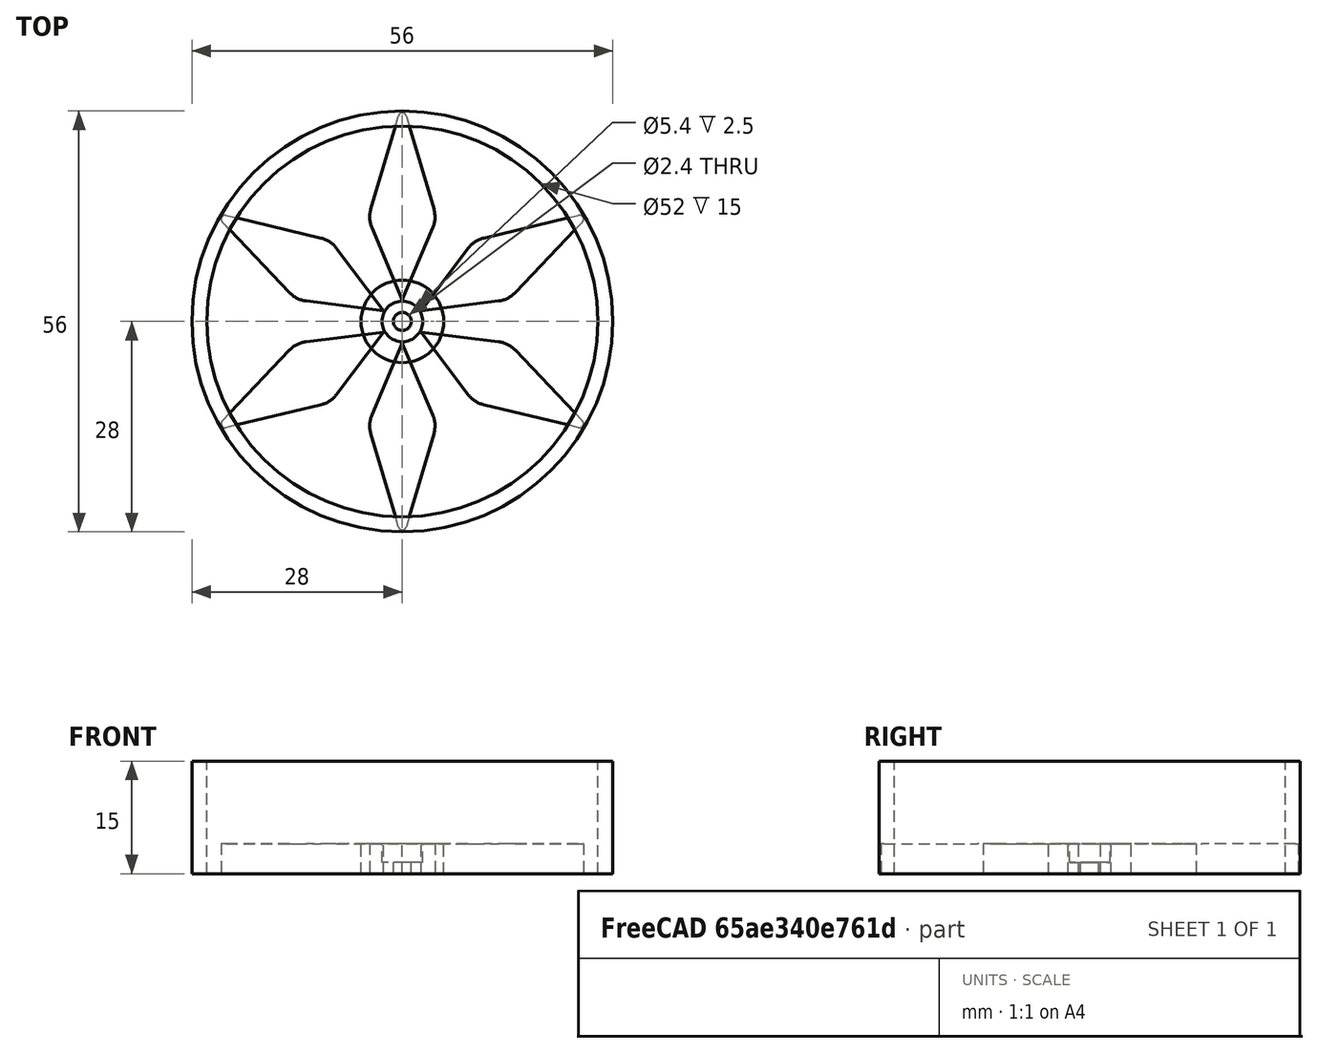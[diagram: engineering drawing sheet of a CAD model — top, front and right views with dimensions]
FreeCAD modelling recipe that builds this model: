
FCSTD DOCUMENT  (FreeCAD 0.16R6712 (Git))
Label: roda_romb
License: All rights reserved
LicenseURL: http://en.wikipedia.org/wiki/All_rights_reserved
objects: Part::Cylinder×5, Part::Cut×3, Sketcher::SketchObject×1, PartDesign::Pad×1, Part::FeaturePython×1
note: 12 computed .brp shape members not serialized (recipe doc carries the construction recipe); baked Part::Feature solids carry a one-line shape summary decoded from their .brp

FEATURE [Part::Cylinder] Cylinder  label="gross"
  Angle = 360
  Height = 4
  Placement = pos=(0,0,-1) rot=(0,0,1;0rad)
  Radius = 5.5
FEATURE [Part::Cylinder] Cylinder001  label="interior"
  Angle = 360
  Height = 6
  Placement = pos=(0,0,0.5) rot=(0,0,1;0rad)
  Radius = 2.7
FEATURE [Part::Cylinder] Cylinder002  label="Cylinder"
  Angle = 360
  Height = 7
  Placement = pos=(0,0,-1) rot=(0,0,1;0rad)
  Radius = 1.2
FEATURE [Part::Cut] Cut
  Base = -> Cylinder
  Tool = -> Cylinder002
FEATURE [Part::Cut] Cut001
  Base = -> Cut
  Placement = pos=(0,0,1) rot=(0,0,1;0rad)
  Tool = -> Cylinder001
FEATURE [Part::Cylinder] Cylinder004  label="fora_gran"
  Angle = 360
  Height = 15
  Placement = pos=(0,0,1) rot=(0,0,1;0rad)
  Radius = 28
FEATURE [Part::Cylinder] Cylinder005  label="forat_gran"
  Angle = 360
  Height = 15
  Placement = pos=(0,0,1) rot=(0,0,1;0rad)
  Radius = 26
FEATURE [Part::Cut] Cut002
  Base = -> Cylinder004
  Placement = pos=(0,0,-1) rot=(0,0,1;0rad)
  Tool = -> Cylinder005
FEATURE [Sketcher::SketchObject] Sketch
  sketch-geometry (7):
    g0: LineSegment StartX=0.518756 StartY=27.3536 StartZ=0 EndX=4.19558 EndY=14.9094 EndZ=0
    g1: LineSegment StartX=4.05671 StartY=12.4595 StartZ=0 EndX=0 EndY=2.87873 EndZ=0
    g2: LineSegment StartX=0 StartY=2.87873 StartZ=0 EndX=-4.05671 EndY=12.4595 EndZ=0
    g3: LineSegment StartX=-4.19558 StartY=14.9094 StartZ=0 EndX=-0.518756 EndY=27.3536 EndZ=0
    g4: ArcOfCircle CenterX=-0.705916 CenterY=13.8783 CenterZ=0 NormalX=0 NormalY=0 NormalZ=1 Radius=3.63879 StartAngle=2.8543 EndAngle=3.54213
    g5: ArcOfCircle CenterX=0.705916 CenterY=13.8783 CenterZ=0 NormalX=0 NormalY=0 NormalZ=1 Radius=3.63879 StartAngle=5.88265 EndAngle=6.57047
    g6: ArcOfCircle CenterX=0 CenterY=27.2004 CenterZ=0 NormalX=0 NormalY=0 NormalZ=1 Radius=0.540926 StartAngle=0.287289 EndAngle=2.8543
  constraints (10):
    c: PointOnObject(g1,g-2)
    c: Coincident(g1,g2)
    c: Tangent(g3,g4) = 1.5708
    c: Tangent(g2,g4) = 1.5708
    c: Tangent(g0,g5) = 1.5708
    c: Tangent(g1,g5) = 1.5708
    c: Tangent(g3,g6) = 1.5708
    c: Tangent(g0,g6) = 1.5708
    c: Symmetric(g2,g1,g-2)
    c: Symmetric(g3,g0,g-2)
FEATURE [PartDesign::Pad] Pad
  Length = 4
  Length2 = 100
  Sketch = -> Sketch
  Type = 0
FEATURE [Part::FeaturePython] Array  # Draft array (typed FeaturePython)
  Angle = 360
  ArrayType = 1
  Axis = (0,0,1)
  Base = -> Pad
  Center = (0,0,0)
  Fuse = false
  IntervalAxis = (0,0,0)
  IntervalX = (1,0,0)
  IntervalY = (0,1,0)
  IntervalZ = (0,0,0)
  NumberPolar = 6
  NumberX = 2
  NumberY = 2
  NumberZ = 1
